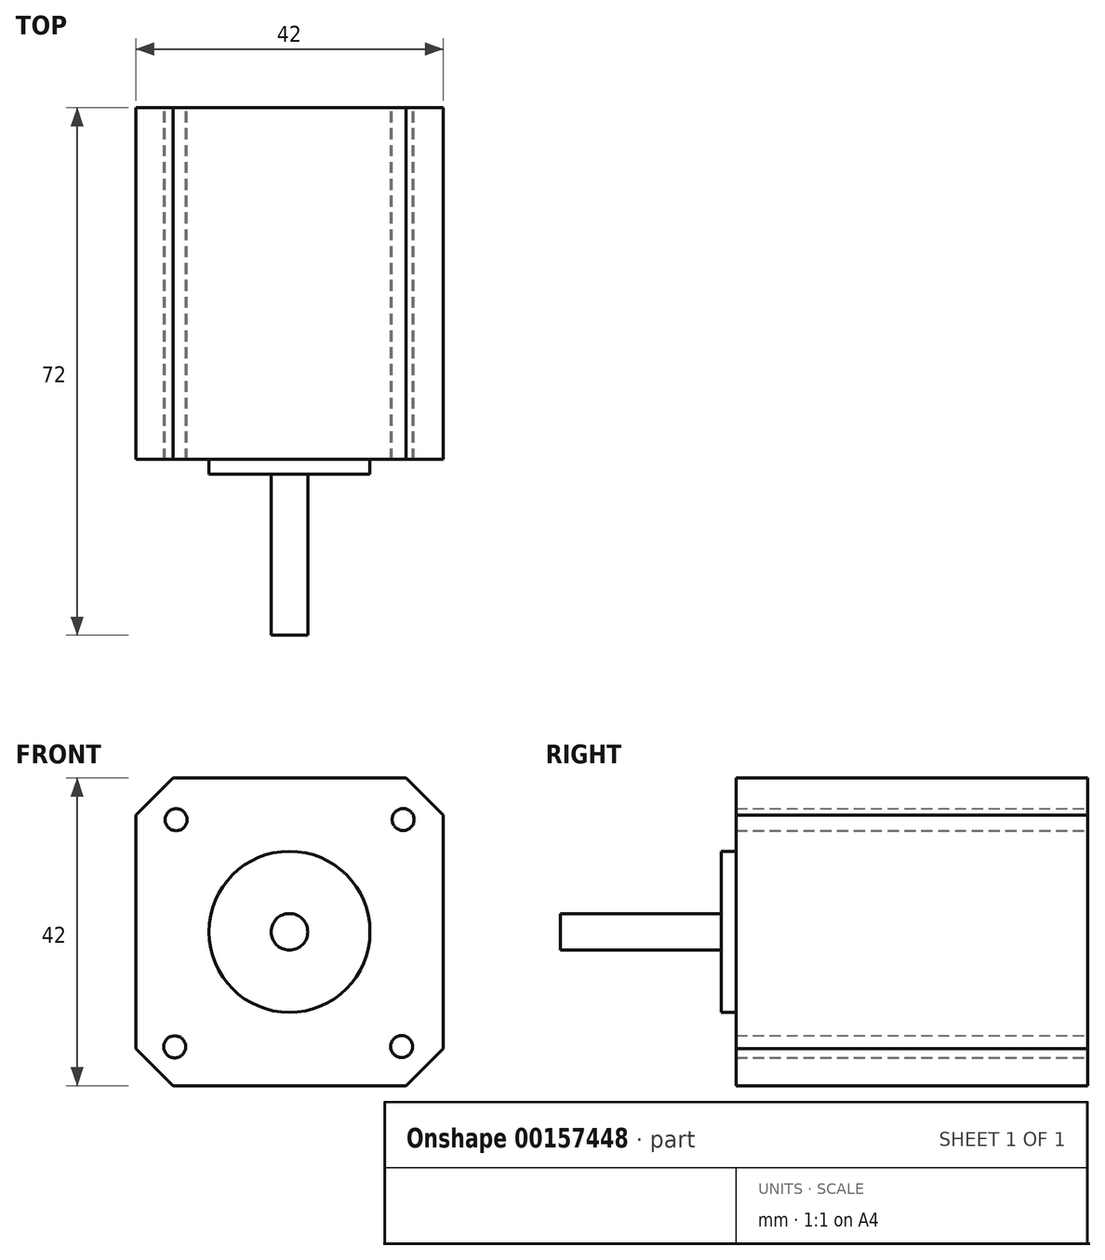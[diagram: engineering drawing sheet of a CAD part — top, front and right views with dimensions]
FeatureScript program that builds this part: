
annotation { "Feature Type Name" : "Feature", "Feature Type Description" : "" }
export const myFeature = defineFeature(function(context is Context, id is Id, definition is map)
    precondition{}
    {
        {
            var Q0;
            Q0=qCreatedBy(makeId("Front.planeOp"),FACE);
            var sketch = newSketch(context, id + "F0", { "sketchPlane" : qUnion([Q0])});
            skLineSegment(sketch, "E0.bottom", {"start": v(21, 21) * mm, "end": v(-21, 21) * mm});
            skLineSegment(sketch, "E0.top", {"start": v(21, -21) * mm, "end": v(-21, -21) * mm});
            skLineSegment(sketch, "E0.left", {"start": v(21, 21) * mm, "end": v(21, -21) * mm});
            skLineSegment(sketch, "E0.right", {"start": v(-21, 21) * mm, "end": v(-21, -21) * mm});
            skPoint(sketch, "E0.middle", {"position": v(0, 0) * mm});
            skCircle(sketch, "E1", {"center": v(-15.47, 15.3) * mm, "radius": 1.5 * mm});
            skCircle(sketch, "E2", {"center": v(15.53, 15.33) * mm, "radius": 1.5 * mm});
            skCircle(sketch, "E3", {"center": v(15.32, -15.67) * mm, "radius": 1.5 * mm});
            skCircle(sketch, "E4", {"center": v(-15.68, -15.7) * mm, "radius": 1.5 * mm});
            skSolve(sketch);
        }
        {
            var Q0;
            Q0=makeQuery(id+"F0.imprint","IMPRINT",FACE,{"disambiguationData":[TD([[makeQuery(id+"F0.imprint","IMPRINT",EDGE,{"derivedFrom":sQuery(id+"F0.wireOp",EDGE,"E0.bottom")}),1.0]])]});
            extrude(context, id + "F1", {"entities" : qUnion([Q0]), "depth" : 48 * mm});
        }
        {
            var Q0;
            Q0=makeQuery(id+"F1.opExtrude","SWEPT_EDGE",EDGE,{"disambiguationData":[OSD([sQuery(id+"F0.wireOp",EDGE,"E0.bottom"),sQuery(id+"F0.wireOp",EDGE,"E0.right")])]});
            var Q1;
            Q1=makeQuery(id+"F1.opExtrude","SWEPT_EDGE",EDGE,{"disambiguationData":[OSD([sQuery(id+"F0.wireOp",EDGE,"E0.bottom"),sQuery(id+"F0.wireOp",EDGE,"E0.left")])]});
            var Q2;
            Q2=makeQuery(id+"F1.opExtrude","SWEPT_EDGE",EDGE,{"disambiguationData":[OSD([sQuery(id+"F0.wireOp",EDGE,"E0.top"),sQuery(id+"F0.wireOp",EDGE,"E0.left")])]});
            var Q3;
            Q3=makeQuery(id+"F1.opExtrude","SWEPT_EDGE",EDGE,{"disambiguationData":[OSD([sQuery(id+"F0.wireOp",EDGE,"E0.top"),sQuery(id+"F0.wireOp",EDGE,"E0.right")])]});
            chamfer(context, id + "F2", {"entities" : qUnion([Q0, Q1, Q2, Q3]), "width" : 5.08 * mm, "tangentPropagation" : true});
        }
        {
            var Q0;
            Q0=makeQuery(id+"F1.opExtrude","CAP_FACE",FACE,{"disambiguationData":[OSD([sQuery(id+"F0.wireOp",EDGE,"E0.bottom"),sQuery(id+"F0.wireOp",EDGE,"E0.top"),sQuery(id+"F0.wireOp",EDGE,"E0.left"),sQuery(id+"F0.wireOp",EDGE,"E0.right"),sQuery(id+"F0.wireOp",EDGE,"E1"),sQuery(id+"F0.wireOp",EDGE,"E2"),sQuery(id+"F0.wireOp",EDGE,"E3"),sQuery(id+"F0.wireOp",EDGE,"E4")])],"isStart":false});
            var sketch = newSketch(context, id + "F3", { "sketchPlane" : qUnion([Q0])});
            skCircle(sketch, "E5", {"center": v(0, 0) * mm, "radius": 11 * mm});
            skSolve(sketch);
        }
        {
            var Q0;
            Q0=makeQuery(id+"F3.imprint","IMPRINT",FACE,{"disambiguationData":[TD([[makeQuery(id+"F3.imprint","IMPRINT",EDGE,{"derivedFrom":sQuery(id+"F3.wireOp",EDGE,"E5")}),1.0]])]});
            extrude(context, id + "F4", {"entities" : qUnion([Q0]), "operationType" : NewBodyOperationType.ADD, "depth" : 2 * mm});
        }
        {
            var Q0;
            Q0=makeQuery(id+"F4.opExtrude","CAP_FACE",FACE,{"disambiguationData":[OSD([sQuery(id+"F3.wireOp",EDGE,"E5")])],"isStart":false});
            var sketch = newSketch(context, id + "F5", { "sketchPlane" : qUnion([Q0])});
            skCircle(sketch, "E6", {"center": v(0, 0) * mm, "radius": 2.5 * mm});
            skSolve(sketch);
        }
        {
            var Q0;
            Q0=makeQuery(id+"F5.imprint","IMPRINT",FACE,{"disambiguationData":[TD([[makeQuery(id+"F5.imprint","IMPRINT",EDGE,{"derivedFrom":sQuery(id+"F5.wireOp",EDGE,"E6")}),1.0]])]});
            extrude(context, id + "F6", {"entities" : qUnion([Q0]), "operationType" : NewBodyOperationType.ADD, "depth" : 22 * mm});
        }
    });
